# Revit family: P200635WX-106c_WRF535SMH_BWZ
name_source: partatom
category: Specialty Equipment
units: mm (PartAtom-declared; Revit-internal decimal feet)

## family parameters
Always vertical = Yes
Cut with Voids When Loaded = No
Enable Cutting in Views = No
Maintain Annotation Orientation = No
Part Type = Normal
Room Calculation Point = No
Round Connector Dimension = Use Diameter
Shared = No
Work Plane-Based = No

## types (3) — shared parameters
Amps = 0 A
Clearance Material = ARCAT - Clearance
Default Elevation = 0"
Depth = 35 1/2"
Description = 36-inch Wide French Door Refrigerator with Crisper Drawer - 25 cu. ft.
Réfrigérateur à portes françaises de 36 po avec tiroir-bac à légumes, 25 pi3
Dimension Guide = https://www.whirlpool.com
https://www.whirlpool.com
Energy Guide = http://access.whirlpool.com Guide&sku=WRF535SMHB&language=EN
http://access.whirlpool.com Guide&sku=WRF535SMHB&language=FR
Family Name = French Door Bottom Mount
Feature 1 = Fingerprint Resistant
Résistant aux traces de doigts
Feature 2 = Full-Width, Temperature-Controlled Drawer
Tiroir à contrôle de température pleine largeur
Feature 3 = Frameless Glass Shelves
Tablettes en verre sans cadre
Height = 70 1/8"
Manufacturer = Whirlpool
Voltage = 0 V
Width = 35 5/8"

## per-type parameters (varying)
| type | Accent Material | Body Material | Door Material | Handle Material | Wheel Material |
| WRF535SMHZ | ARCAT - Metal - Steel -Gray | ARCAT - Metal - Steel -Gray | ARCAT - Metal - Steel - Stainless | ARCAT - Metal - Steel -Gray - Light | ARCAT - Metal - Steel -Gray |
| WRF535SMHB | ARCAT - Metal - Steel - Black | ARCAT - Metal - Steel - Black | ARCAT - Metal - Steel - Black | ARCAT - Metal - Steel - Black - Dark | ARCAT - Plastic - Black - Dark |
| WRF535SMHW | ARCAT - Metal - Steel - White | ARCAT - Metal - Steel - White | ARCAT - Metal - Steel - White | ARCAT - Metal - Steel - White | ARCAT - Plastic - White |

note: column(s) folded — value = type name in every type: Model

## geometry (parser evidence)
native form markers: Sweep x6
no freeform markers — native parametric forms only
